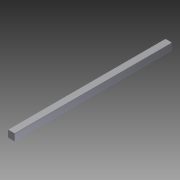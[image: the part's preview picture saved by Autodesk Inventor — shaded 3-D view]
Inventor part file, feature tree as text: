
AUTODESK INVENTOR PART (.ipt)
format: ipt  version: 2012 (Build 160160000, 160)  size: 120,320 bytes
history: native  units: in
note: dims shown in document units (in); Inventor stores cm internally (conversion verified against a paired STEP export)
features: other x1, imported_body x1, plane x1, split x1
ambient origin geometry x8: Origin, YZ Plane, XZ Plane, XY Plane, X Axis, Y Axis, Z Axis, Center Point
feature tree (4):
  parser-record x1  (decoder bookkeeping rows leaked as tree rows — omitted from the tree; the rows remain in map.json)
  imported_body  "Base1"
  plane  "Work Plane1"
  split  "Split1"
